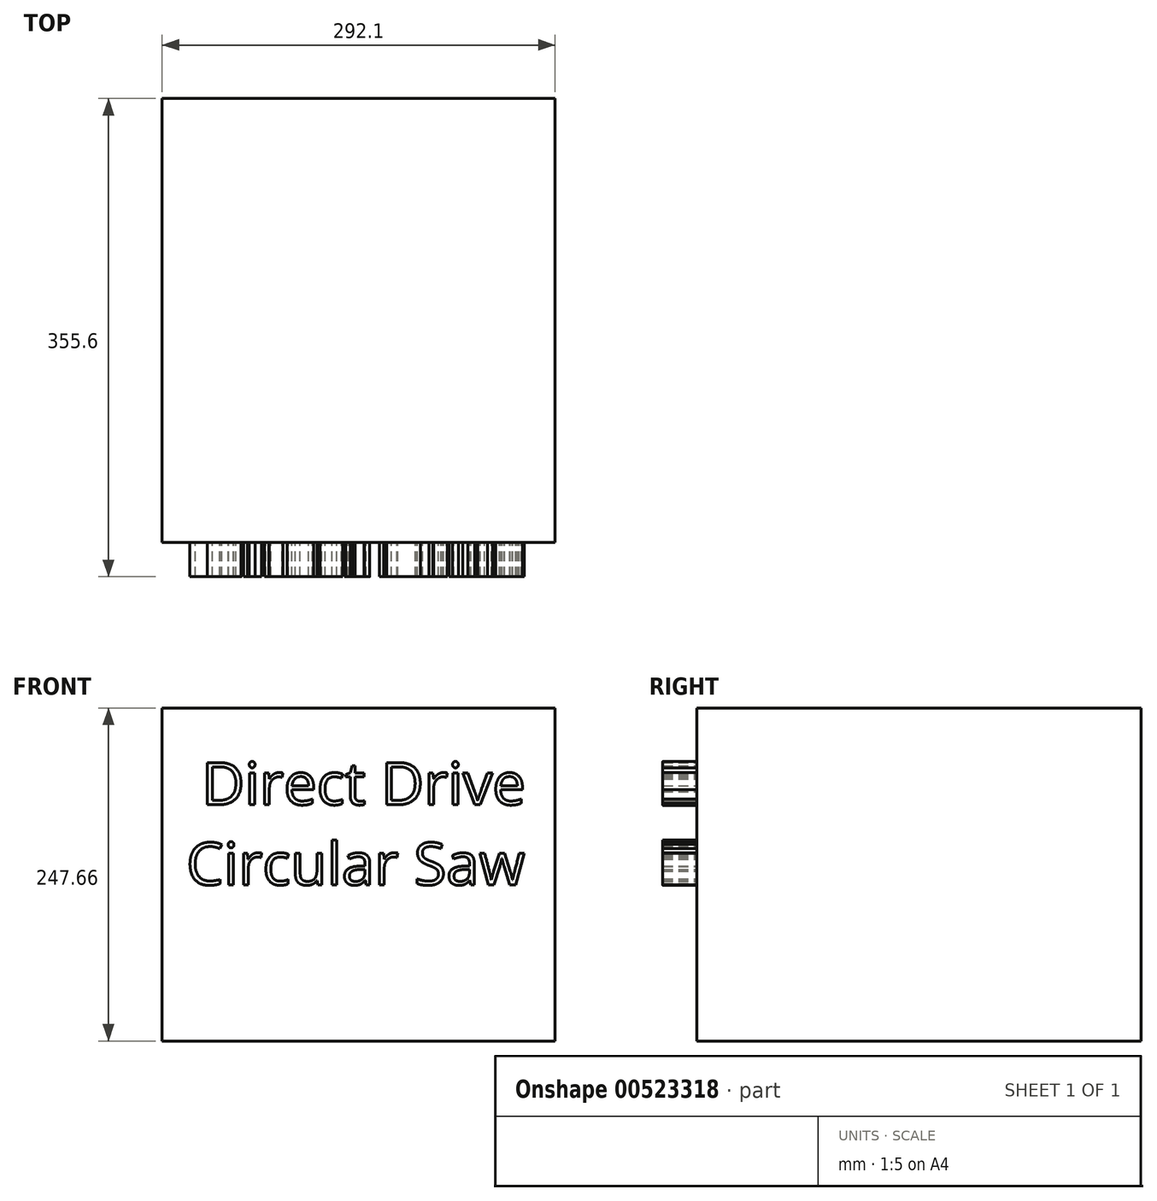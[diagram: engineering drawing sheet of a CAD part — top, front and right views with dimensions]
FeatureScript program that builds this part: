
annotation { "Feature Type Name" : "Feature", "Feature Type Description" : "" }
export const myFeature = defineFeature(function(context is Context, id is Id, definition is map)
    precondition{}
    {
        {
            var Q0;
            Q0=qCreatedBy(makeId("Front.planeOp"),FACE);
            var sketch = newSketch(context, id + "F0", { "sketchPlane" : qUnion([Q0])});
            skLineSegment(sketch, "E0.bottom", {"start": v(146.05, 123.83) * mm, "end": v(-146.05, 123.83) * mm});
            skLineSegment(sketch, "E0.top", {"start": v(146.05, -123.83) * mm, "end": v(-146.05, -123.83) * mm});
            skLineSegment(sketch, "E0.left", {"start": v(146.05, 123.83) * mm, "end": v(146.05, -123.83) * mm});
            skLineSegment(sketch, "E0.right", {"start": v(-146.05, 123.83) * mm, "end": v(-146.05, -123.83) * mm});
            skPoint(sketch, "E0.middle", {"position": v(0, 0) * mm});
            skSolve(sketch);
        }
        {
            var Q0;
            Q0=makeQuery(id+"F0.imprint","IMPRINT",FACE,{"disambiguationData":[TD([[makeQuery(id+"F0.imprint","IMPRINT",EDGE,{"derivedFrom":sQuery(id+"F0.wireOp",EDGE,"E0.bottom")}),1.0]])]});
            extrude(context, id + "F1", {"entities" : qUnion([Q0]), "depth" : 330.2 * mm, "offsetDistance" : 25.4 * mm});
        }
        {
            var Q0;
            Q0=makeQuery(id+"F1.opExtrude","CAP_FACE",FACE,{"disambiguationData":[OSD([sQuery(id+"F0.wireOp",EDGE,"E0.bottom"),sQuery(id+"F0.wireOp",EDGE,"E0.top"),sQuery(id+"F0.wireOp",EDGE,"E0.left"),sQuery(id+"F0.wireOp",EDGE,"E0.right")])],"isStart":false});
            var sketch = newSketch(context, id + "F2", { "sketchPlane" : qUnion([Q0])});
            skText(sketch, "E1", { "text": " Direct Drive\nCircular Saw", "fontName": "OpenSans-Regular.ttf"});
            const initialGuessF2  = {"E1": [-0.1281, 0.05189, 1, 0, 0.03155]};
            skSetInitialGuess(sketch, initialGuessF2);
            skSolve(sketch);
        }
        {
            var Q0;
            Q0 = qSketchRegion(id + "F2", true);
            extrude(context, id + "F3", {"entities" : qUnion([Q0]), "operationType" : NewBodyOperationType.ADD, "depth" : 25.4 * mm, "offsetDistance" : 25.4 * mm});
        }
    });
